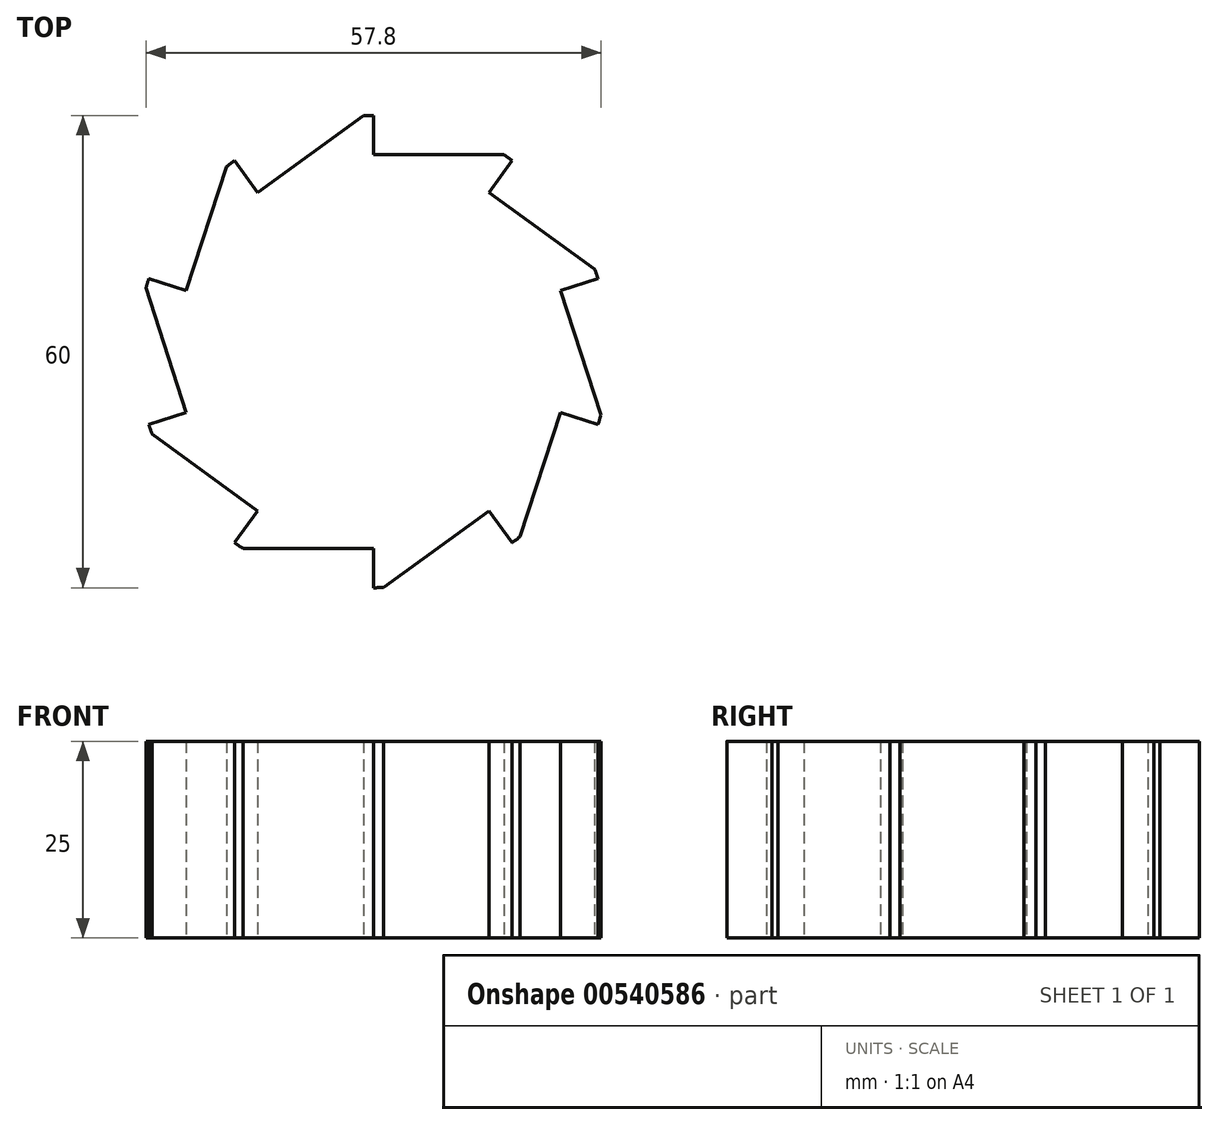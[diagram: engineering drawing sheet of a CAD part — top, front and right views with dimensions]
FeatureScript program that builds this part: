
annotation { "Feature Type Name" : "Feature", "Feature Type Description" : "" }
export const myFeature = defineFeature(function(context is Context, id is Id, definition is map)
    precondition{}
    {
        {
            var Q0;
            Q0=qCreatedBy(makeId("Top.planeOp"),FACE);
            var sketch = newSketch(context, id + "F0", { "sketchPlane" : qUnion([Q0])});
            skArc(sketch, "E0", {"start": v(0, 30) * mm, "mid": v(-0.64, 30) * mm, "end": v(-1.28, 29.97) * mm});
            skLineSegment(sketch, "E1", {"start": v(0, 30) * mm, "end": v(0, 25) * mm});
            skLineSegment(sketch, "E2", {"start": v(0, 25) * mm, "end": v(16.58, 25) * mm});
            skLineSegment(sketch, "E3.1.0", {"start": v(-14.7, 20.23) * mm, "end": v(-1.28, 29.97) * mm});
            skLineSegment(sketch, "E3.1.1", {"start": v(-17.63, 24.27) * mm, "end": v(-14.7, 20.23) * mm});
            skLineSegment(sketch, "E3.2.0", {"start": v(-23.78, 7.73) * mm, "end": v(-18.65, 23.5) * mm});
            skLineSegment(sketch, "E3.2.1", {"start": v(-28.53, 9.27) * mm, "end": v(-23.78, 7.73) * mm});
            skLineSegment(sketch, "E3.3.0", {"start": v(-23.78, -7.73) * mm, "end": v(-28.9, 8.05) * mm});
            skLineSegment(sketch, "E3.3.1", {"start": v(-28.53, -9.27) * mm, "end": v(-23.78, -7.73) * mm});
            skLineSegment(sketch, "E3.4.0", {"start": v(-14.7, -20.23) * mm, "end": v(-28.11, -10.48) * mm});
            skLineSegment(sketch, "E3.4.1", {"start": v(-17.63, -24.27) * mm, "end": v(-14.7, -20.23) * mm});
            skLineSegment(sketch, "E3.5.0", {"start": v(0, -25) * mm, "end": v(-16.58, -25) * mm});
            skLineSegment(sketch, "E3.5.1", {"start": v(0, -30) * mm, "end": v(0, -25) * mm});
            skLineSegment(sketch, "E3.6.0", {"start": v(14.7, -20.23) * mm, "end": v(1.28, -29.97) * mm});
            skLineSegment(sketch, "E3.6.1", {"start": v(17.63, -24.27) * mm, "end": v(14.7, -20.23) * mm});
            skLineSegment(sketch, "E3.7.0", {"start": v(23.78, -7.73) * mm, "end": v(18.65, -23.5) * mm});
            skLineSegment(sketch, "E3.7.1", {"start": v(28.53, -9.27) * mm, "end": v(23.78, -7.73) * mm});
            skLineSegment(sketch, "E3.8.0", {"start": v(23.78, 7.73) * mm, "end": v(28.9, -8.05) * mm});
            skLineSegment(sketch, "E3.8.1", {"start": v(28.53, 9.27) * mm, "end": v(23.78, 7.73) * mm});
            skLineSegment(sketch, "E3.9.0", {"start": v(14.7, 20.23) * mm, "end": v(28.11, 10.48) * mm});
            skLineSegment(sketch, "E3.9.1", {"start": v(17.63, 24.27) * mm, "end": v(14.7, 20.23) * mm});
            skArc(sketch, "E4.trimOffspring", {"start": v(17.63, 24.27) * mm, "mid": v(17.11, 24.64) * mm, "end": v(16.58, 25) * mm});
            skArc(sketch, "E5.trimOffspring", {"start": v(28.53, 9.27) * mm, "mid": v(28.33, 9.88) * mm, "end": v(28.11, 10.48) * mm});
            skArc(sketch, "E6.trimOffspring", {"start": v(28.53, -9.27) * mm, "mid": v(28.72, -8.66) * mm, "end": v(28.9, -8.05) * mm});
            skArc(sketch, "E7.trimOffspring", {"start": v(17.63, -24.27) * mm, "mid": v(18.15, -23.89) * mm, "end": v(18.65, -23.5) * mm});
            skArc(sketch, "E8.trimOffspring", {"start": v(0, -30) * mm, "mid": v(0.64, -30) * mm, "end": v(1.28, -29.97) * mm});
            skArc(sketch, "E9.trimOffspring", {"start": v(-17.63, -24.27) * mm, "mid": v(-17.11, -24.64) * mm, "end": v(-16.58, -25) * mm});
            skArc(sketch, "E10.trimOffspring", {"start": v(-28.53, -9.27) * mm, "mid": v(-28.33, -9.88) * mm, "end": v(-28.11, -10.48) * mm});
            skArc(sketch, "E11.trimOffspring", {"start": v(-28.53, 9.27) * mm, "mid": v(-28.72, 8.66) * mm, "end": v(-28.9, 8.05) * mm});
            skArc(sketch, "E12.trimOffspring", {"start": v(-17.63, 24.27) * mm, "mid": v(-18.15, 23.89) * mm, "end": v(-18.65, 23.5) * mm});
            skSolve(sketch);
        }
        {
            var Q0;
            Q0=makeQuery(id+"F0.imprint","IMPRINT",FACE,{"disambiguationData":[TD([[makeQuery(id+"F0.imprint","IMPRINT",EDGE,{"derivedFrom":sQuery(id+"F0.wireOp",EDGE,"E0")}),1.0]])]});
            extrude(context, id + "F1", {"entities" : qUnion([Q0]), "depth" : 25 * mm, "offsetDistance" : 25 * mm});
        }
    });
